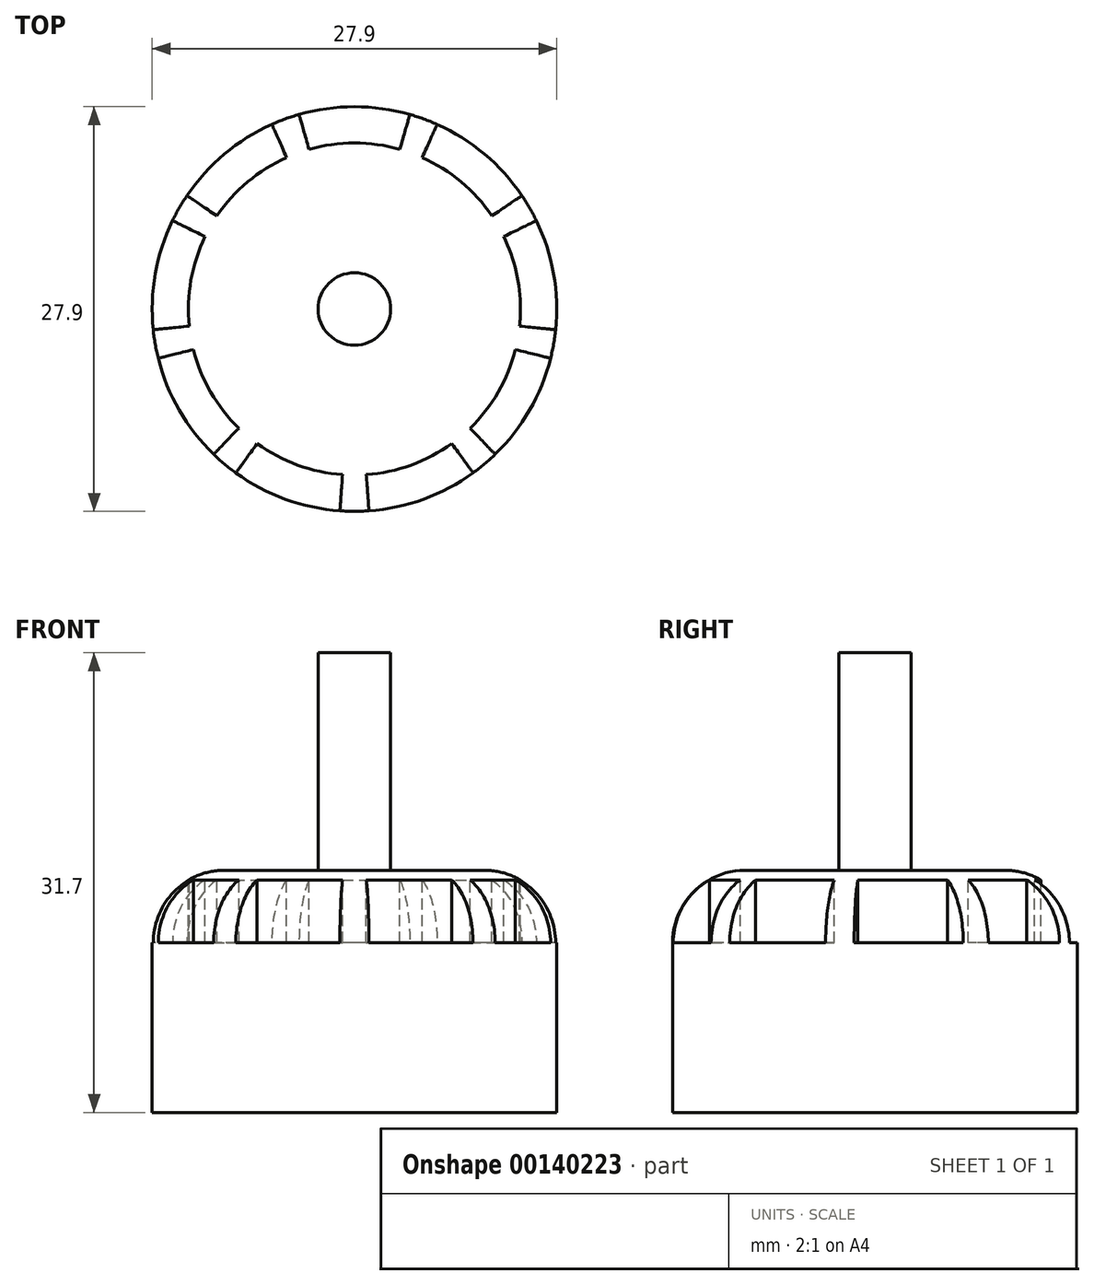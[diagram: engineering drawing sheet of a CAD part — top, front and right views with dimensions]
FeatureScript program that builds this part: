
annotation { "Feature Type Name" : "Feature", "Feature Type Description" : "" }
export const myFeature = defineFeature(function(context is Context, id is Id, definition is map)
    precondition{}
    {
        {
            var Q0;
            Q0=qCreatedBy(makeId("Top.planeOp"),FACE);
            var sketch = newSketch(context, id + "F0", { "sketchPlane" : qUnion([Q0])});
            skCircle(sketch, "E0", {"center": v(0, 0) * mm, "radius": 13.95 * mm});
            skSolve(sketch);
        }
        {
            var Q0;
            Q0 = qSketchRegion(id + "F0", true);
            extrude(context, id + "F1", {"entities" : qUnion([Q0]), "depth" : (31.7 - 15) * mm});
        }
        {
            var Q0;
            Q0=makeQuery(id+"F1.opExtrude","CAP_EDGE",EDGE,{"disambiguationData":[OSD([sQuery(id+"F0.wireOp",EDGE,"E0")])],"isStart":false});
            fillet(context, id + "F2", {"entities" : qUnion([Q0]), "radius" : 5 * mm, "tangentPropagation" : true, "allowEdgeOverflow" : false});
        }
        {
            var Q0;
            Q0=makeQuery(id+"F1.opExtrude","CAP_FACE",FACE,{"disambiguationData":[OSD([sQuery(id+"F0.wireOp",EDGE,"E0")])],"isStart":false});
            var sketch = newSketch(context, id + "F3", { "sketchPlane" : qUnion([Q0])});
            skArc(sketch, "E1", {"start": v(-3.13, 11.01) * mm, "mid": v(-1.58, 11.34) * mm, "end": v(0, 11.45) * mm});
            skLineSegment(sketch, "E2", {"start": v(0, 0) * mm, "end": v(0, 11.45) * mm, "construction": true});
            skArc(sketch, "E3", {"start": v(-3.82, 13.42) * mm, "mid": v(-1.93, 13.82) * mm, "end": v(0, 13.95) * mm});
            skLineSegment(sketch, "E4", {"start": v(-3.82, 13.42) * mm, "end": v(-3.13, 11.01) * mm});
            skArc(sketch, "E5.MirrorCS", {"start": v(3.82, 13.42) * mm, "mid": v(1.93, 13.82) * mm, "end": v(0, 13.95) * mm});
            skLineSegment(sketch, "E6.MirrorCS", {"start": v(3.82, 13.42) * mm, "end": v(3.13, 11.01) * mm});
            skArc(sketch, "E7.MirrorCS", {"start": v(3.13, 11.01) * mm, "mid": v(1.58, 11.34) * mm, "end": v(0, 11.45) * mm});
            skLineSegment(sketch, "E8.1.0", {"start": v(-11.55, 7.82) * mm, "end": v(-9.48, 6.42) * mm});
            skArc(sketch, "E8.1.1", {"start": v(-9.48, 6.42) * mm, "mid": v(-8.5, 7.67) * mm, "end": v(-7.36, 8.77) * mm});
            skArc(sketch, "E8.1.2", {"start": v(-4.68, 10.45) * mm, "mid": v(-6.08, 9.7) * mm, "end": v(-7.36, 8.77) * mm});
            skLineSegment(sketch, "E8.1.3", {"start": v(-5.7, 12.73) * mm, "end": v(-4.68, 10.45) * mm});
            skArc(sketch, "E8.1.4", {"start": v(-5.7, 12.73) * mm, "mid": v(-7.4, 11.82) * mm, "end": v(-8.97, 10.69) * mm});
            skArc(sketch, "E8.1.5", {"start": v(-11.55, 7.82) * mm, "mid": v(-10.36, 9.34) * mm, "end": v(-8.97, 10.69) * mm});
            skLineSegment(sketch, "E8.2.0", {"start": v(-13.88, -1.43) * mm, "end": v(-11.39, -1.17) * mm});
            skArc(sketch, "E8.2.1", {"start": v(-11.39, -1.17) * mm, "mid": v(-11.44, 0.41) * mm, "end": v(-11.28, 1.99) * mm});
            skArc(sketch, "E8.2.2", {"start": v(-10.3, 5) * mm, "mid": v(-10.9, 3.53) * mm, "end": v(-11.28, 1.99) * mm});
            skLineSegment(sketch, "E8.2.3", {"start": v(-12.55, 6.1) * mm, "end": v(-10.3, 5) * mm});
            skArc(sketch, "E8.2.4", {"start": v(-12.55, 6.1) * mm, "mid": v(-13.27, 4.3) * mm, "end": v(-13.74, 2.42) * mm});
            skArc(sketch, "E8.2.5", {"start": v(-13.88, -1.43) * mm, "mid": v(-13.94, 0.5) * mm, "end": v(-13.74, 2.42) * mm});
            skLineSegment(sketch, "E9.2.3.0", {"start": v(-9.7, -10.02) * mm, "end": v(-7.97, -8.22) * mm});
            skArc(sketch, "E9.3.3.0", {"start": v(-7.97, -8.22) * mm, "mid": v(-9.03, -7.04) * mm, "end": v(-9.92, -5.72) * mm});
            skArc(sketch, "E9.7.3.0", {"start": v(-11.1, -2.8) * mm, "mid": v(-10.61, -4.3) * mm, "end": v(-9.92, -5.72) * mm});
            skLineSegment(sketch, "E9.11.3.0", {"start": v(-13.53, -3.4) * mm, "end": v(-11.1, -2.8) * mm});
            skArc(sketch, "E9.14.3.0", {"start": v(-13.53, -3.4) * mm, "mid": v(-12.93, -5.24) * mm, "end": v(-12.08, -6.97) * mm});
            skArc(sketch, "E9.18.3.0", {"start": v(-9.7, -10.02) * mm, "mid": v(-11, -8.58) * mm, "end": v(-12.08, -6.97) * mm});
            skLineSegment(sketch, "E9.2.4.0", {"start": v(-1, -13.91) * mm, "end": v(-0.82, -11.42) * mm});
            skArc(sketch, "E9.3.4.0", {"start": v(-0.82, -11.42) * mm, "mid": v(-2.4, -11.2) * mm, "end": v(-3.92, -10.76) * mm});
            skArc(sketch, "E9.7.4.0", {"start": v(-6.71, -9.28) * mm, "mid": v(-5.37, -10.11) * mm, "end": v(-3.92, -10.76) * mm});
            skLineSegment(sketch, "E9.11.4.0", {"start": v(-8.18, -11.3) * mm, "end": v(-6.71, -9.28) * mm});
            skArc(sketch, "E9.14.4.0", {"start": v(-8.18, -11.3) * mm, "mid": v(-6.54, -12.32) * mm, "end": v(-4.77, -13.1) * mm});
            skArc(sketch, "E9.18.4.0", {"start": v(-1, -13.91) * mm, "mid": v(-2.91, -13.64) * mm, "end": v(-4.77, -13.1) * mm});
            skLineSegment(sketch, "E9.2.5.0", {"start": v(8.18, -11.3) * mm, "end": v(6.71, -9.28) * mm});
            skArc(sketch, "E9.3.5.0", {"start": v(6.71, -9.28) * mm, "mid": v(5.37, -10.11) * mm, "end": v(3.92, -10.76) * mm});
            skArc(sketch, "E9.7.5.0", {"start": v(0.82, -11.42) * mm, "mid": v(2.4, -11.2) * mm, "end": v(3.92, -10.76) * mm});
            skLineSegment(sketch, "E9.11.5.0", {"start": v(1, -13.91) * mm, "end": v(0.82, -11.42) * mm});
            skArc(sketch, "E9.14.5.0", {"start": v(1, -13.91) * mm, "mid": v(2.91, -13.64) * mm, "end": v(4.77, -13.1) * mm});
            skArc(sketch, "E9.18.5.0", {"start": v(8.18, -11.3) * mm, "mid": v(6.54, -12.32) * mm, "end": v(4.77, -13.1) * mm});
            skLineSegment(sketch, "E9.2.6.0", {"start": v(13.53, -3.4) * mm, "end": v(11.1, -2.8) * mm});
            skArc(sketch, "E9.3.6.0", {"start": v(11.1, -2.8) * mm, "mid": v(10.61, -4.3) * mm, "end": v(9.92, -5.73) * mm});
            skArc(sketch, "E9.7.6.0", {"start": v(7.97, -8.22) * mm, "mid": v(9.03, -7.04) * mm, "end": v(9.92, -5.73) * mm});
            skLineSegment(sketch, "E9.11.6.0", {"start": v(9.7, -10.02) * mm, "end": v(7.97, -8.22) * mm});
            skArc(sketch, "E9.14.6.0", {"start": v(9.7, -10.02) * mm, "mid": v(11, -8.58) * mm, "end": v(12.08, -6.98) * mm});
            skArc(sketch, "E9.18.6.0", {"start": v(13.53, -3.4) * mm, "mid": v(12.93, -5.24) * mm, "end": v(12.08, -6.98) * mm});
            skLineSegment(sketch, "E9.2.7.0", {"start": v(12.55, 6.1) * mm, "end": v(10.3, 5) * mm});
            skArc(sketch, "E9.3.7.0", {"start": v(10.3, 5) * mm, "mid": v(10.9, 3.53) * mm, "end": v(11.28, 1.99) * mm});
            skArc(sketch, "E9.7.7.0", {"start": v(11.39, -1.17) * mm, "mid": v(11.44, 0.41) * mm, "end": v(11.28, 1.99) * mm});
            skLineSegment(sketch, "E9.11.7.0", {"start": v(13.88, -1.43) * mm, "end": v(11.39, -1.17) * mm});
            skArc(sketch, "E9.14.7.0", {"start": v(13.88, -1.43) * mm, "mid": v(13.94, 0.5) * mm, "end": v(13.74, 2.42) * mm});
            skArc(sketch, "E9.18.7.0", {"start": v(12.55, 6.1) * mm, "mid": v(13.27, 4.3) * mm, "end": v(13.74, 2.42) * mm});
            skLineSegment(sketch, "E10.2.8.0", {"start": v(5.7, 12.73) * mm, "end": v(4.68, 10.45) * mm});
            skArc(sketch, "E10.3.8.0", {"start": v(4.68, 10.45) * mm, "mid": v(6.08, 9.7) * mm, "end": v(7.36, 8.77) * mm});
            skArc(sketch, "E10.7.8.0", {"start": v(9.48, 6.42) * mm, "mid": v(8.5, 7.67) * mm, "end": v(7.36, 8.77) * mm});
            skLineSegment(sketch, "E10.11.8.0", {"start": v(11.55, 7.82) * mm, "end": v(9.48, 6.42) * mm});
            skArc(sketch, "E10.14.8.0", {"start": v(11.55, 7.82) * mm, "mid": v(10.36, 9.34) * mm, "end": v(8.97, 10.69) * mm});
            skArc(sketch, "E10.18.8.0", {"start": v(5.7, 12.73) * mm, "mid": v(7.4, 11.82) * mm, "end": v(8.97, 10.69) * mm});
            skSolve(sketch);
        }
        {
            var Q0;
            Q0 = qSketchRegion(id + "F3", true);
            extrude(context, id + "F4", {"entities" : qUnion([Q0]), "operationType" : NewBodyOperationType.REMOVE, "oppositeDirection" : true, "depth" : 5 * mm});
        }
        {
            var Q0;
            Q0=makeQuery(id+"F1.opExtrude","CAP_FACE",FACE,{"disambiguationData":[OSD([sQuery(id+"F0.wireOp",EDGE,"E0")])],"isStart":false});
            var sketch = newSketch(context, id + "F5", { "sketchPlane" : qUnion([Q0])});
            skCircle(sketch, "E11", {"center": v(0, 0) * mm, "radius": 2.5 * mm});
            skSolve(sketch);
        }
        {
            var Q0;
            Q0 = qSketchRegion(id + "F5", true);
            extrude(context, id + "F6", {"entities" : qUnion([Q0]), "operationType" : NewBodyOperationType.ADD, "depth" : 15 * mm});
        }
    });
